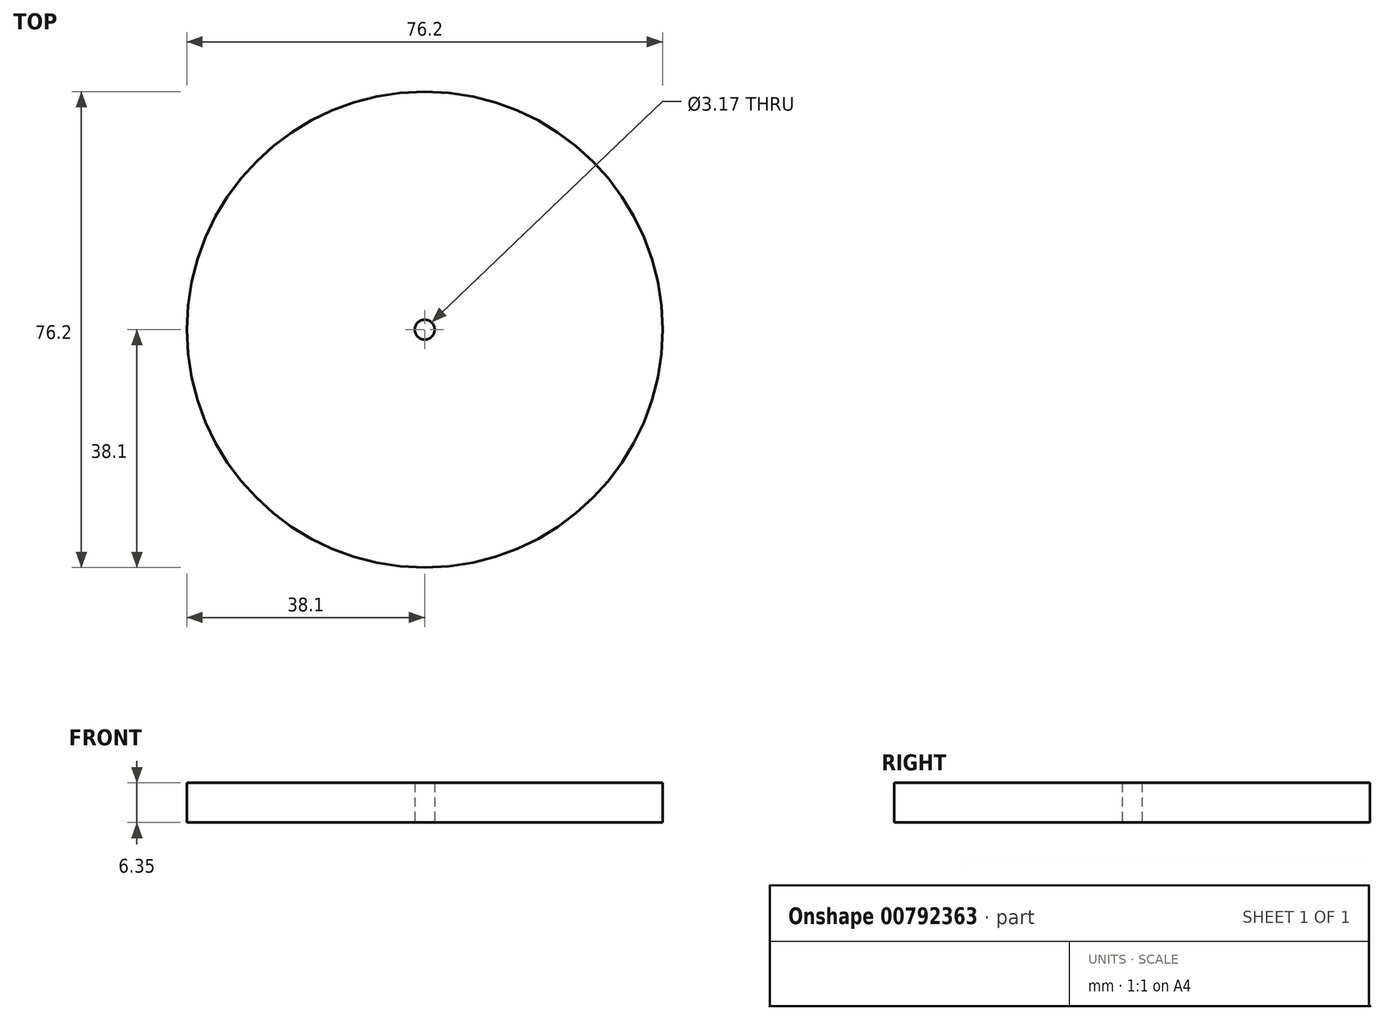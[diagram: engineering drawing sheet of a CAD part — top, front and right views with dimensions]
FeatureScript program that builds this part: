
annotation { "Feature Type Name" : "Feature", "Feature Type Description" : "" }
export const myFeature = defineFeature(function(context is Context, id is Id, definition is map)
    precondition{}
    {
        {
            var Q0;
            Q0=qCreatedBy(makeId("Top.planeOp"),FACE);
            var sketch = newSketch(context, id + "F0", { "sketchPlane" : qUnion([Q0])});
            skCircle(sketch, "E0", {"center": v(0, 0) * mm, "radius": 38.1 * mm});
            skCircle(sketch, "E1", {"center": v(0, 0) * mm, "radius": 1.59 * mm});
            skSolve(sketch);
        }
        {
            var Q0;
            Q0 = qSketchRegion(id + "F0", true);
            extrude(context, id + "F1", {"entities" : qUnion([Q0]), "depth" : 6.35 * mm, "offsetDistance" : 25.4 * mm});
        }
    });
